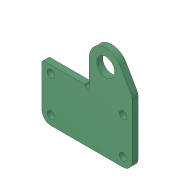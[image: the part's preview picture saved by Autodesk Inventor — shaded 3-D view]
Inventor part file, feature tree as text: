
AUTODESK INVENTOR PART (.ipt)
format: ipt  version: 2019.4 (Build 234330000, 330)  size: 208,896 bytes
history: native  units: mm
features: sketch x2, hole x2, other x1, extrude x1
ambient origin geometry x8: Origin, YZ Plane, XZ Plane, XY Plane, X Axis, Y Axis, Z Axis, Center Point
bodies: Body1 (feature_tree)
feature tree (6):
  other  "ソリッド1"
  sketch  "スケッチ1"
  sketch  "スケッチ2"
  extrude  "押し出し1"  Depth=60.0mm
  hole  "穴1"  [1 undecoded]
  hole  "穴2"  [1 undecoded]
note: 2 required parameter values undecoded (feature->parameter linkage not recoverable at this tier; creation-order binding heuristic only, values carry confidence <= 0.55)
